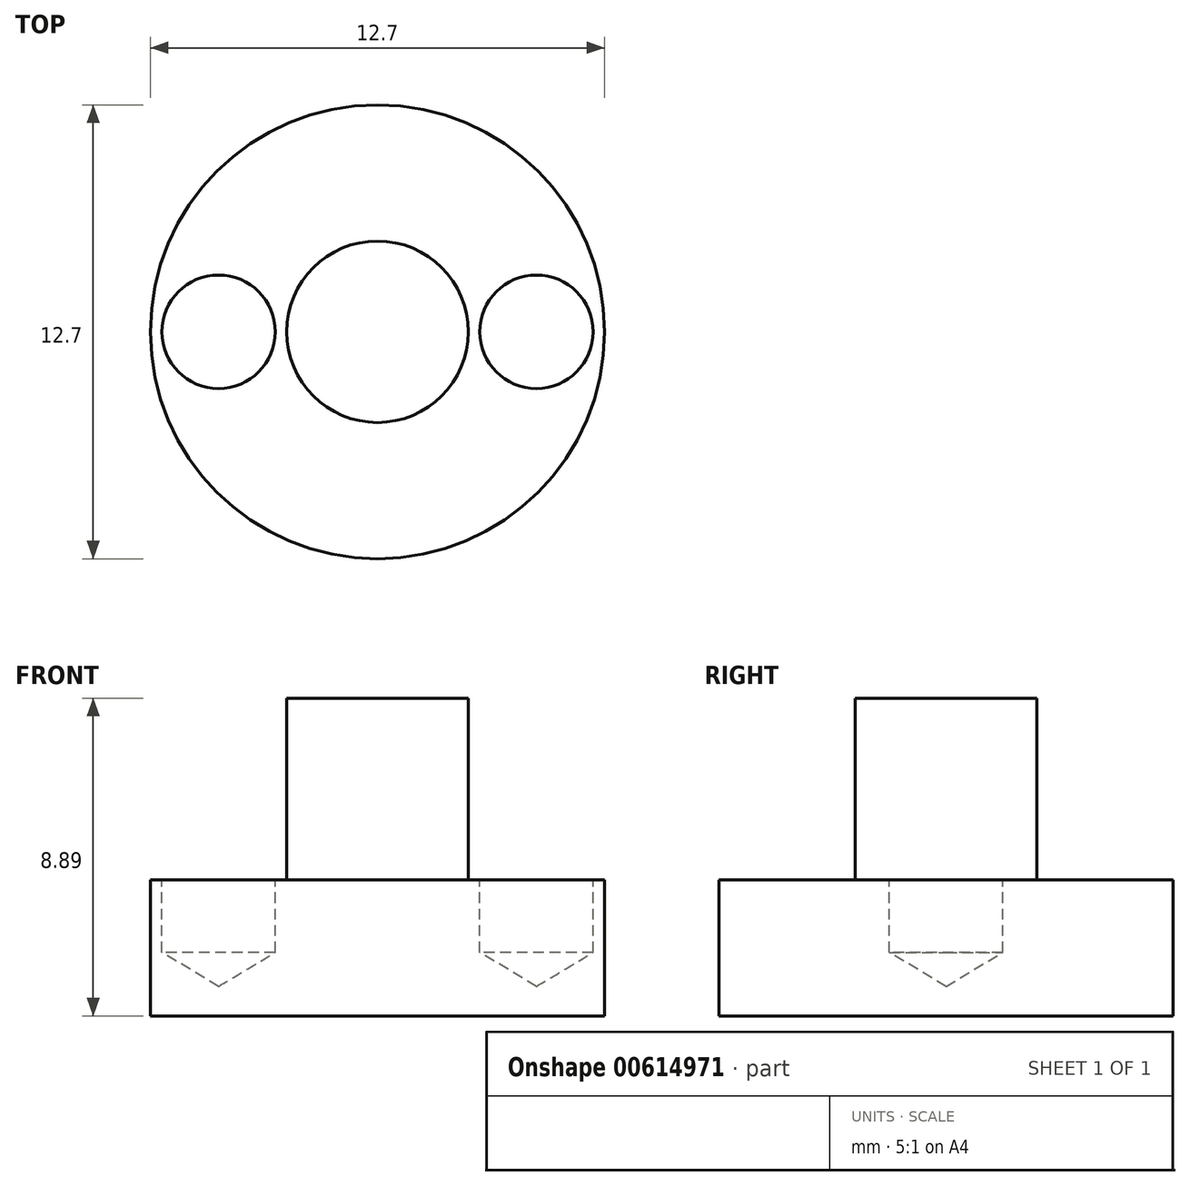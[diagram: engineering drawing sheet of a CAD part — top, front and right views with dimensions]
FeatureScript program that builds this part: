
annotation { "Feature Type Name" : "Feature", "Feature Type Description" : "" }
export const myFeature = defineFeature(function(context is Context, id is Id, definition is map)
    precondition{}
    {
        {
            var Q0;
            Q0=qCreatedBy(makeId("Top.planeOp"),FACE);
            var sketch = newSketch(context, id + "F0", { "sketchPlane" : qUnion([Q0])});
            skCircle(sketch, "E0", {"center": v(0, 0) * mm, "radius": 6.35 * mm});
            skSolve(sketch);
        }
        {
            var Q0;
            Q0 = qSketchRegion(id + "F0", true);
            extrude(context, id + "F1", {"entities" : qUnion([Q0]), "depth" : 3.8 * mm, "offsetDistance" : 25.4 * mm});
        }
        {
            var Q0;
            Q0=makeQuery(id+"F1.opExtrude","CAP_FACE",FACE,{"disambiguationData":[OSD([sQuery(id+"F0.wireOp",EDGE,"E0")])],"isStart":false});
            var sketch = newSketch(context, id + "F2", { "sketchPlane" : qUnion([Q0])});
            skCircle(sketch, "E1", {"center": v(0, 0) * mm, "radius": 2.54 * mm});
            skSolve(sketch);
        }
        {
            var Q0;
            Q0 = qSketchRegion(id + "F2", true);
            extrude(context, id + "F3", {"entities" : qUnion([Q0]), "operationType" : NewBodyOperationType.ADD, "depth" : 5.08 * mm, "offsetDistance" : 25.4 * mm});
        }
        {
            var Q0;
            Q0=makeQuery(id+"F1.opExtrude","CAP_FACE",FACE,{"disambiguationData":[OSD([sQuery(id+"F0.wireOp",EDGE,"E0")])],"isStart":false});
            var sketch = newSketch(context, id + "F4", { "sketchPlane" : qUnion([Q0])});
            skPoint(sketch, "E2", {"position": v(-4.44, 0) * mm});
            skSolve(sketch);
        }
        {
            var Q0;
            Q0=makeQuery(id+"F4.imprint","IMPRINT",FACE,{"disambiguationData":[TD([[makeQuery(id+"F4.imprint","IMPRINT",EDGE,{"derivedFrom":makeQuery(id+"F1.opExtrude","CAP_EDGE",EDGE,{"disambiguationData":[OSD([sQuery(id+"F0.wireOp",EDGE,"E0")])],"isStart":false})}),1.0]])]});
            var sketch = newSketch(context, id + "F5", { "sketchPlane" : qUnion([Q0])});
            skPoint(sketch, "E3", {"position": v(4.45, 0) * mm});
            skSolve(sketch);
        }
        {
            var Q0;
            Q0=sQuery(id+"F4.wireOp",VERTEX,"E2");
            var Q1;
            Q1=makeQuery(id+"F1.opExtrude","SWEPT_BODY",BODY,{"disambiguationData":[OSD([sQuery(id+"F0.wireOp",EDGE,"E0")])]});
            hole(context, id + "F6", {"style" : HoleStyle.SIMPLE, "endStyle" : HoleEndStyle.BLIND, "holeDiameter" : 3.17 * mm, "majorDiameter" : 6.35 * mm, "holeDepth" : 2.03 * mm, "isTappedThrough" : true, "tappedDepth" : 12.7 * mm, "tapClearance" : 3, "locations" : qUnion([Q0]), "scope" : qUnion([Q1])});
        }
        {
            var Q0;
            Q0=sQuery(id+"F5.wireOp",VERTEX,"E3");
            var Q1;
            Q1=makeQuery(id+"F1.opExtrude","SWEPT_BODY",BODY,{"disambiguationData":[OSD([sQuery(id+"F0.wireOp",EDGE,"E0")])]});
            hole(context, id + "F7", {"style" : HoleStyle.SIMPLE, "endStyle" : HoleEndStyle.BLIND, "holeDiameter" : 3.17 * mm, "majorDiameter" : 6.35 * mm, "holeDepth" : 2.03 * mm, "isTappedThrough" : true, "tappedDepth" : 12.7 * mm, "tapClearance" : 3, "locations" : qUnion([Q0]), "scope" : qUnion([Q1])});
        }
    });
